# Revit family: FantiniCosmi_BIM_AP20048
name_source: partatom
category: Generic Models
units: mm (PartAtom-declared; Revit-internal decimal feet)

## family parameters
Always vertical = Yes
Can host rebar = No
Cut with Voids When Loaded = No
Part Type = Normal
Room Calculation Point = No
Round Connector Dimension = Use Diameter
Shared = No
Work Plane-Based = No

## types (1)
- Standard
     Efficienza di recupero EN13141-7 = 86,1 %
     Portata aria V3/V2/V1 = 620 / 355 / 165  mc/h
    Classe di filtrazione = ePM1 70
    Corrente assorbita  = 3.5 A
    Default Elevation = 0 mm  [stored 0 ft]
    Description = ASPIRCOMFORT CLASS 620H
    Efficienza di recupero EN308  = 91,8 %
    Grado di protezione = IP X0
    Numero Scambiatori = 2
    Numero Ventilatori = 2+1
    Part Number = AP20048
    Potenza assorbita  = 340 W
    Pressione utile = 15 Pa
    Tensione di alimentazione = 230V / 1 / 50 Hz

note: [stored X ft] marks values corroborated as IEEE doubles in the binary element streams (Revit-internal decimal feet)

## geometry (parser evidence)
native form markers: Sweep x3
no freeform markers — native parametric forms only
